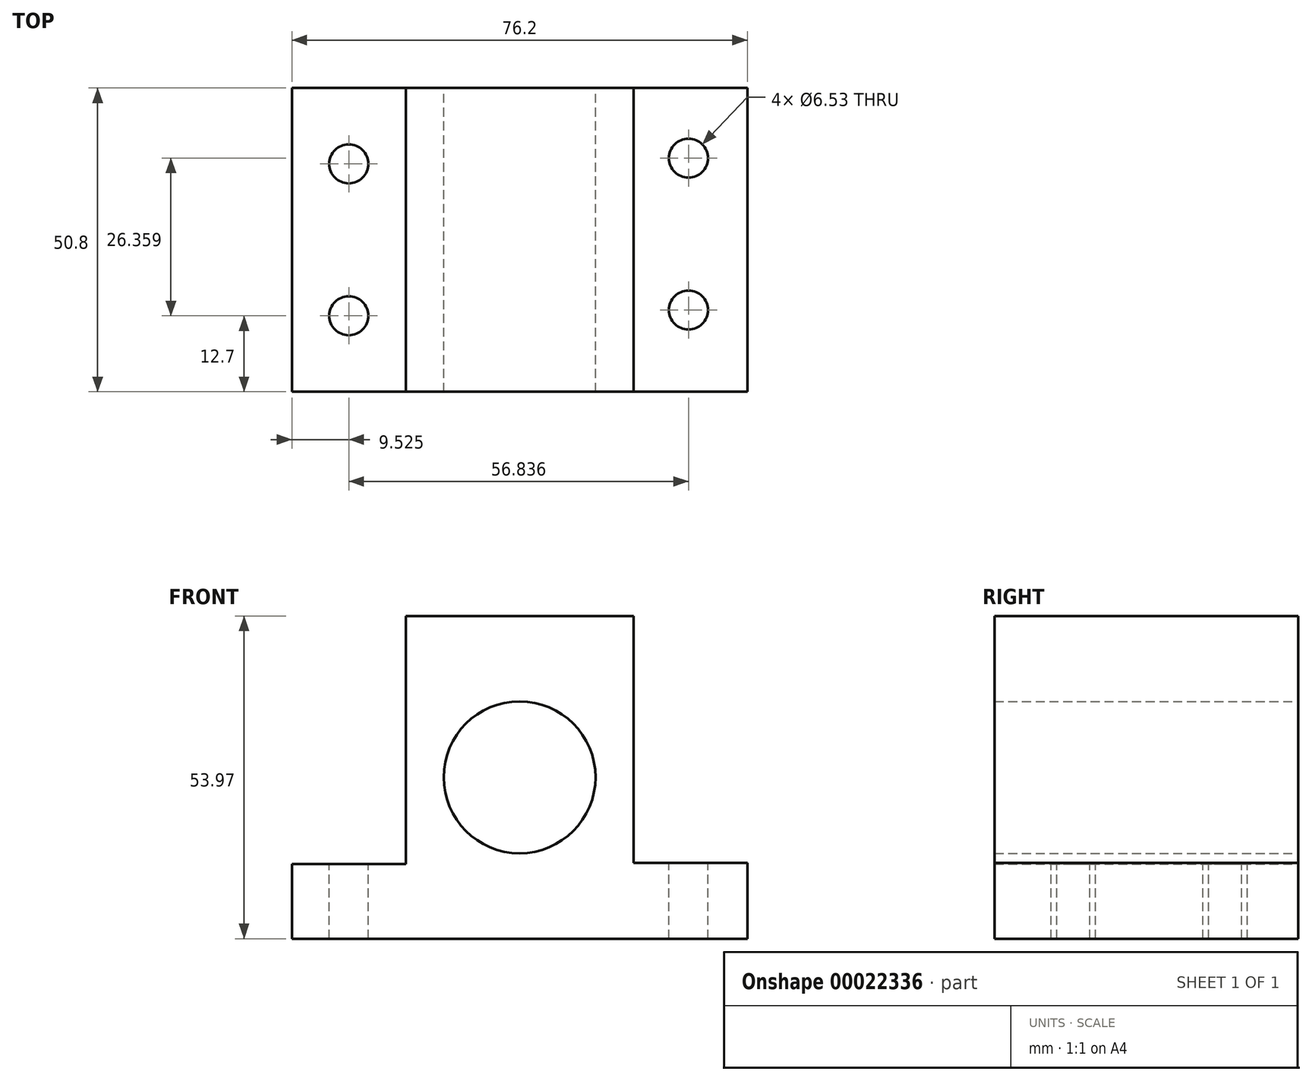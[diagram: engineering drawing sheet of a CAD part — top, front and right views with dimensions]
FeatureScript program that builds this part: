
annotation { "Feature Type Name" : "Feature", "Feature Type Description" : "" }
export const myFeature = defineFeature(function(context is Context, id is Id, definition is map)
    precondition{}
    {
        {
            var Q0;
            Q0=qCreatedBy(makeId("Front.planeOp"),FACE);
            var sketch = newSketch(context, id + "F0", { "sketchPlane" : qUnion([Q0])});
            skLineSegment(sketch, "E0", {"start": v(-38.1, -20.7) * mm, "end": v(-38.1, -8) * mm});
            skLineSegment(sketch, "E1", {"start": v(-38.1, -8) * mm, "end": v(-19.05, -8) * mm});
            skLineSegment(sketch, "E2", {"start": v(-19.05, -8) * mm, "end": v(-19.05, 33.47) * mm});
            skLineSegment(sketch, "E3", {"start": v(-19.05, 33.47) * mm, "end": v(19.05, 33.47) * mm});
            skLineSegment(sketch, "E4", {"start": v(19.05, 33.47) * mm, "end": v(19.05, -7.8) * mm});
            skLineSegment(sketch, "E5", {"start": v(19.05, -7.8) * mm, "end": v(38.1, -7.8) * mm});
            skLineSegment(sketch, "E6", {"start": v(38.1, -7.8) * mm, "end": v(38.1, -20.5) * mm});
            skLineSegment(sketch, "E7", {"start": v(38.1, -20.5) * mm, "end": v(-38.1, -20.5) * mm});
            skLineSegment(sketch, "E8", {"start": v(0, 46.69) * mm, "end": v(0, -48.35) * mm});
            skCircle(sketch, "E9", {"center": v(0, 6.48) * mm, "radius": 12.7 * mm});
            skSolve(sketch);
        }
        {
            var Q0;
            {var subQ9=sQuery(id+"F0.wireOp",EDGE,"E4");Q0=makeQuery(id+"F0.imprint","IMPRINT",FACE,{"disambiguationData":[TD([[makeQuery(id+"F0.imprint","IMPRINT",EDGE,{"derivedFrom":subQ9}),-1.0]])]});}
            var Q1;
            {var subQ11=sQuery(id+"F0.wireOp",EDGE,"E1");Q1=makeQuery(id+"F0.imprint","IMPRINT",FACE,{"disambiguationData":[TD([[makeQuery(id+"F0.imprint","IMPRINT",EDGE,{"derivedFrom":subQ11}),-1.0]])]});}
            extrude(context, id + "F1", {"entities" : qUnion([Q0, Q1]), "depth" : 50.8 * mm});
        }
        {
            var Q0;
            Q0=makeQuery(id+"F1.opExtrude","SWEPT_FACE",FACE,{"disambiguationData":[OSD([sQuery(id+"F0.wireOp",EDGE,"E1")])]});
            var sketch = newSketch(context, id + "F2", { "sketchPlane" : qUnion([Q0])});
            skCircle(sketch, "E10", {"center": v(-28.58, -12.7) * mm, "radius": 3.26 * mm});
            skCircle(sketch, "E11", {"center": v(-28.58, -38.1) * mm, "radius": 3.26 * mm});
            skSolve(sketch);
        }
        {
            var Q0;
            Q0=makeQuery(id+"F1.opExtrude","SWEPT_FACE",FACE,{"disambiguationData":[OSD([sQuery(id+"F0.wireOp",EDGE,"E5")])]});
            var sketch = newSketch(context, id + "F3", { "sketchPlane" : qUnion([Q0])});
            skCircle(sketch, "E12", {"center": v(28.26, -11.74) * mm, "radius": 3.26 * mm});
            skCircle(sketch, "E13", {"center": v(28.26, -37.14) * mm, "radius": 3.26 * mm});
            skSolve(sketch);
        }
        {
            var Q0;
            Q0=makeQuery(id+"F2.imprint","IMPRINT",FACE,{"disambiguationData":[TD([[makeQuery(id+"F2.imprint","IMPRINT",EDGE,{"derivedFrom":sQuery(id+"F2.wireOp",EDGE,"E11")}),1.0]])]});
            var Q1;
            Q1=makeQuery(id+"F2.imprint","IMPRINT",FACE,{"disambiguationData":[TD([[makeQuery(id+"F2.imprint","IMPRINT",EDGE,{"derivedFrom":sQuery(id+"F2.wireOp",EDGE,"E10")}),1.0]])]});
            var Q2;
            Q2=makeQuery(id+"F3.imprint","IMPRINT",FACE,{"disambiguationData":[TD([[makeQuery(id+"F3.imprint","IMPRINT",EDGE,{"derivedFrom":sQuery(id+"F3.wireOp",EDGE,"E12")}),1.0]])]});
            var Q3;
            Q3=makeQuery(id+"F3.imprint","IMPRINT",FACE,{"disambiguationData":[TD([[makeQuery(id+"F3.imprint","IMPRINT",EDGE,{"derivedFrom":sQuery(id+"F3.wireOp",EDGE,"E13")}),1.0]])]});
            extrude(context, id + "F4", {"entities" : qUnion([Q0, Q1, Q2, Q3]), "operationType" : NewBodyOperationType.REMOVE, "endBound" : BoundingType.THROUGH_ALL, "oppositeDirection" : true, "depth" : 25.4 * mm});
        }
    });
